# Revit family: Sanitary_Showers_AXOR_35368USA-AXOR-ShowerSolutions-Overhead-s_009
name_source: partatom
category: Plumbing Fixtures
revit_build: Autodesk Revit 2018 (Build: 20170223_1515(x64)
units: mm (PartAtom-declared; Revit-internal decimal feet)

## family parameters
Always vertical = No
Cut with Voids When Loaded = No
OmniClass Number = 23.31.17.19
OmniClass Title = Shower Head Fixtures
Part Type = Normal
Room Calculation Point = No
Round Connector Dimension = Use Diameter
Shared = No
Work Plane-Based = Yes

## types (5) — shared parameters
Always visible = Yes
BIMobject category = Showers
Default Elevation = 1219.2 mm  [stored 4 ft]
Description = AXOR ShowerSolutions Overhead shower 220 1jet 1.75 GPM
Design country = Germany
EAN code = 4059625404294
Edition number = 1
GTIN code = https://4059625404294
IFC Classification = Sanitary Terminal
Installation instructions = https://www.axor-design.com
Manufacturer = AXOR
Manufacturer country = Germany
Manufacturer name = AXOR
Model = 35368USA
OmniClass Code = 23-31 17 19
OmniClass Description = Shower Head Fixtures
Product Guid = 0ebaee58-465b-48ad-8a71-d0d146ac39a5
Product SKU = 35368USA
Product data url = https://bimobject.com
Product family = AXOR ShowerSolutions
Product group = Overhead showers
Product name = 35368USA AXOR ShowerSolutions Overhead shower 220 1jet 1.75 GPM
Product url = https://www.axor-design.com
QR code = https://bimobject.com
URL = https://www.axor-design.com
Water Inlet = 13 mm
Water Inlet Description = Water Inlet 12.7mm
Weight Net (Kg) = 1.7

## per-type parameters (varying)
| type | Material 1 |
| 821 Brushed Nickel | AXOR - Metal - 821 Brushed Nickel |
| 671 Matt Black | AXOR - Metal - 671 Matt Black |
| 341 Brushed Black Chrome | AXOR - Metal - 341 Brushed Black Chrome |
| 251 Brushed Gold Optic | AXOR - Metal - 251 Brushed Gold Optic |
| 001 Chrome | AXOR - Metal - 001 Chrome |

note: [stored X ft] marks values corroborated as IEEE doubles in the binary element streams (Revit-internal decimal feet)

## geometry (parser evidence)
native form markers: Sweep x3
no freeform markers — native parametric forms only
